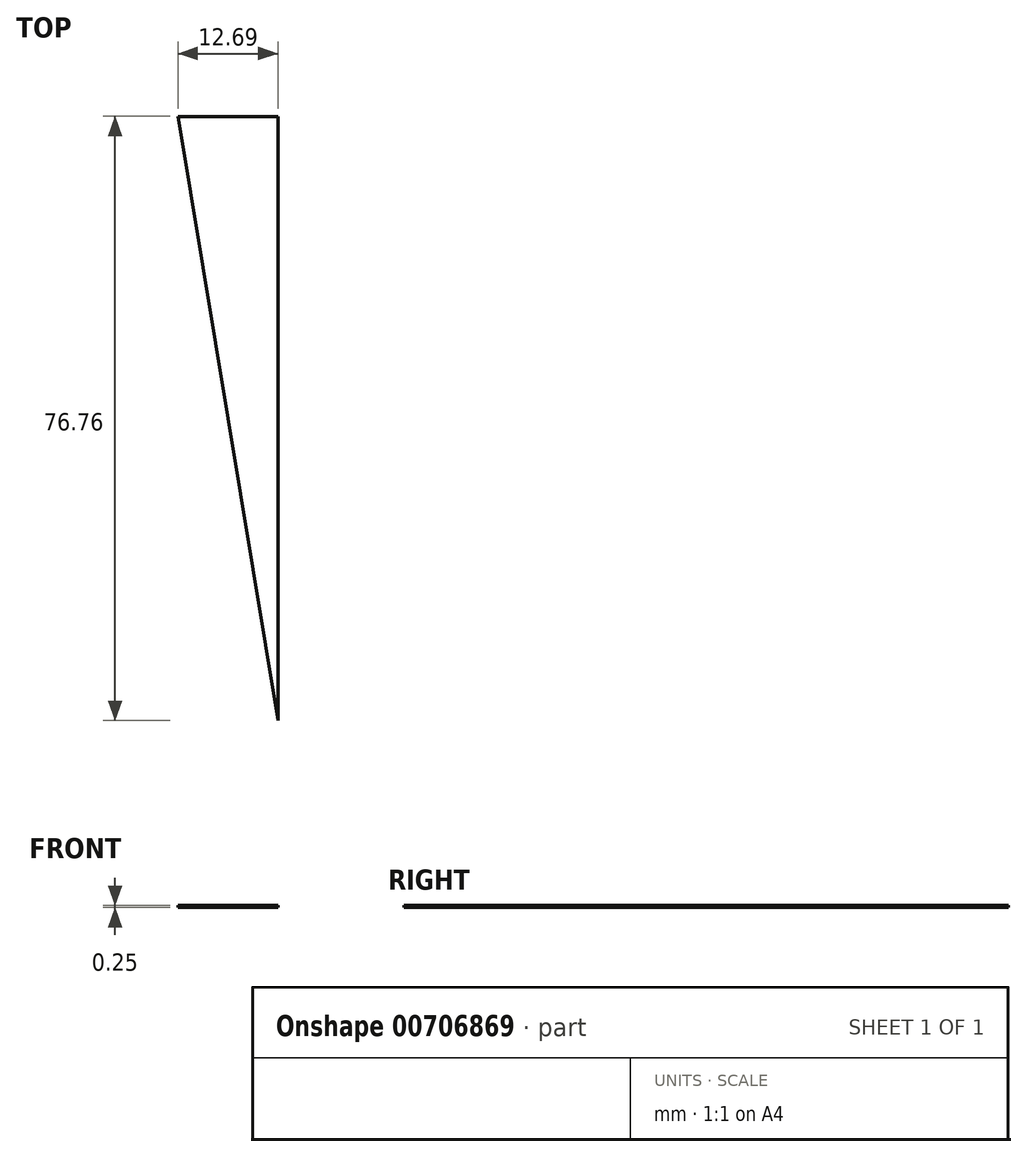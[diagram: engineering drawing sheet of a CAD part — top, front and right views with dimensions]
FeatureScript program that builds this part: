
annotation { "Feature Type Name" : "Feature", "Feature Type Description" : "" }
export const myFeature = defineFeature(function(context is Context, id is Id, definition is map)
    precondition{}
    {
        {
            var Q0;
            Q0=qCreatedBy(makeId("Top.planeOp"),FACE);
            var sketch = newSketch(context, id + "F0", { "sketchPlane" : qUnion([Q0])});
            skLineSegment(sketch, "E0.right", {"start": v(70.05, 29.6) * mm, "end": v(70.05, -47.16) * mm});
            skLineSegment(sketch, "E1", {"start": v(57.36, 29.6) * mm, "end": v(70.05, -47.16) * mm});
            skLineSegment(sketch, "E2", {"start": v(57.36, 29.6) * mm, "end": v(70.05, 29.6) * mm});
            skSolve(sketch);
        }
        {
            var Q0;
            Q0 = qSketchRegion(id + "F0", true);
            extrude(context, id + "F1", {"entities" : qUnion([Q0]), "depth" : 0.25 * mm, "offsetDistance" : 25.4 * mm});
        }
    });
